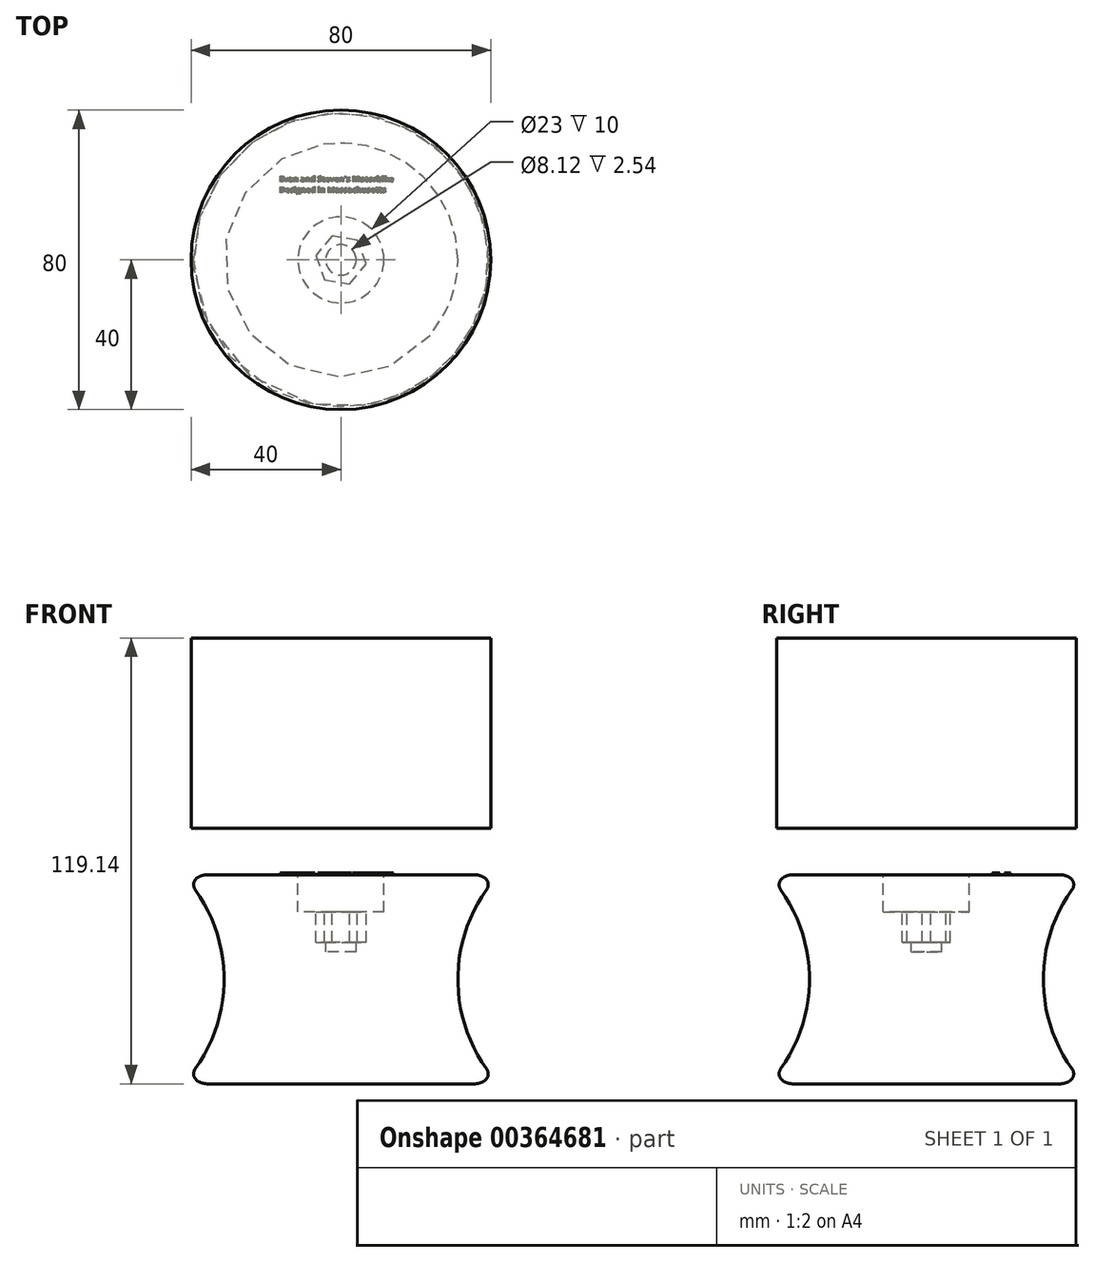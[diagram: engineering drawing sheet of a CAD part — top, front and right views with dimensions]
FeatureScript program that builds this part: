
annotation { "Feature Type Name" : "Feature", "Feature Type Description" : "" }
export const myFeature = defineFeature(function(context is Context, id is Id, definition is map)
    precondition{}
    {
        {
            var Q0;
            Q0=qCreatedBy(makeId("Top.planeOp"),FACE);
            var sketch = newSketch(context, id + "F0", { "sketchPlane" : qUnion([Q0])});
            skCircle(sketch, "E0", {"center": v(0, 0) * mm, "radius": 40 * mm});
            skCircle(sketch, "E1.cCircle", {"center": v(0, 0) * mm, "radius": 5.92 * mm, "construction": true});
            skLineSegment(sketch, "E1.0", {"start": v(-2.36, 6.42) * mm, "end": v(4.38, 5.25) * mm});
            skLineSegment(sketch, "E1.1", {"start": v(4.38, 5.25) * mm, "end": v(6.74, -1.17) * mm});
            skLineSegment(sketch, "E1.2", {"start": v(6.74, -1.17) * mm, "end": v(2.36, -6.42) * mm});
            skLineSegment(sketch, "E1.3", {"start": v(2.36, -6.42) * mm, "end": v(-4.38, -5.25) * mm});
            skLineSegment(sketch, "E1.4", {"start": v(-4.38, -5.25) * mm, "end": v(-6.74, 1.17) * mm});
            skLineSegment(sketch, "E1.5", {"start": v(-6.74, 1.17) * mm, "end": v(-2.36, 6.42) * mm});
            skPoint(sketch, "E1.0.midPoint", {"position": v(1.01, 5.84) * mm});
            skSolve(sketch);
        }
        {
            var Q0;
            Q0=qSketchRegion(id+"F0",true);
            var Q1;
            Q1=makeQuery(id+"F0.imprint","IMPRINT",FACE,{"disambiguationData":[TD([[makeQuery(id+"F0.imprint","IMPRINT",EDGE,{"derivedFrom":sQuery(id+"F0.wireOp",EDGE,"E1.0")}),-1.0]])]});
            extrude(context, id + "F1", {"entities" : qUnion([Q0, Q1]), "depth" : 50.8 * mm});
        }
        {
            var Q0;
            Q0=makeQuery(id+"F1.opExtrude","CAP_FACE",FACE,{"disambiguationData":[OSD([sQuery(id+"F0.wireOp",EDGE,"E0"),sQuery(id+"F0.wireOp",EDGE,"E1.0"),sQuery(id+"F0.wireOp",EDGE,"E1.1"),sQuery(id+"F0.wireOp",EDGE,"E1.2"),sQuery(id+"F0.wireOp",EDGE,"E1.3"),sQuery(id+"F0.wireOp",EDGE,"E1.4"),sQuery(id+"F0.wireOp",EDGE,"E1.5")])],"isStart":true});
            var sketch = newSketch(context, id + "F2", { "sketchPlane" : qUnion([Q0])});
            skCircle(sketch, "E2", {"center": v(0, 0) * mm, "radius": 11.5 * mm});
            skSolve(sketch);
        }
        {
            var Q0;
            Q0=qCreatedBy(makeId("Right.planeOp"),FACE);
            var sketch = newSketch(context, id + "F3", { "sketchPlane" : qUnion([Q0])});
            skLineSegment(sketch, "E3.left", {"start": v(-40, -12.46) * mm, "end": v(-40, -68.34) * mm});
            skArc(sketch, "E4", {"start": v(-40, -65.8) * mm, "mid": v(-31.22, -40.4) * mm, "end": v(-40, -15) * mm});
            skLineSegment(sketch, "E5.bottom", {"start": v(-40, -12.46) * mm, "end": v(0, -12.46) * mm});
            skLineSegment(sketch, "E5.top", {"start": v(-40, -68.34) * mm, "end": v(0, -68.34) * mm});
            skLineSegment(sketch, "E5.right", {"start": v(0, -12.46) * mm, "end": v(0, -68.34) * mm});
            skSolve(sketch);
        }
        {
            var Q0;
            {var subQ1=sQuery(id+"F3.wireOp",EDGE,"E4");Q0=makeQuery(id+"F3.imprint","IMPRINT",FACE,{"disambiguationData":[TD([[makeQuery(id+"F3.imprint","IMPRINT",EDGE,{"derivedFrom":subQ1}),-1.0]])]});}
            var Q1;
            Q1=sQuery(id+"F3.wireOp",EDGE,"E5.right");
            revolve(context, id + "F4", {"entities" : qUnion([Q0]), "axis" : qUnion([Q1]), "revolveType" : RevolveType.FULL});
        }
        {
            var Q0;
            Q0=makeQuery(id+"F4.opRevolve","SWEPT_FACE",FACE,{"disambiguationData":[OSD([sQuery(id+"F3.wireOp",EDGE,"E5.bottom")])]});
            var sketch = newSketch(context, id + "F5", { "sketchPlane" : qUnion([Q0])});
            skLineSegment(sketch, "E6.0.0", {"start": v(-2.36, 6.42) * mm, "end": v(-6.74, 1.17) * mm});
            skLineSegment(sketch, "E6.0.1", {"start": v(-6.74, 1.17) * mm, "end": v(-4.38, -5.25) * mm});
            skLineSegment(sketch, "E6.0.2", {"start": v(-4.38, -5.25) * mm, "end": v(2.36, -6.42) * mm});
            skLineSegment(sketch, "E6.0.3", {"start": v(2.36, -6.42) * mm, "end": v(6.74, -1.17) * mm});
            skLineSegment(sketch, "E6.0.4", {"start": v(6.74, -1.17) * mm, "end": v(4.38, 5.25) * mm});
            skLineSegment(sketch, "E6.0.5", {"start": v(4.38, 5.25) * mm, "end": v(-2.36, 6.42) * mm});
            skCircle(sketch, "E7.0", {"center": v(0, 0) * mm, "radius": 11.5 * mm});
            skCircle(sketch, "E8", {"center": v(0, 0) * mm, "radius": 4.06 * mm});
            skText(sketch, "E9", { "text": "Evan & Steven\'s Capstone", "fontName": "OpenSans-Bold.ttf"});
            const initialGuessF5  = {"E9": [-0.01963, 0.0219, 1, 0, 0.00215]};
            skSetInitialGuess(sketch, initialGuessF5);
            skSolve(sketch);
        }
        {
            var Q0;
            Q0=makeQuery(id+"F5.imprint","IMPRINT",FACE,{"disambiguationData":[TD([[makeQuery(id+"F5.imprint","IMPRINT",EDGE,{"derivedFrom":sQuery(id+"F5.wireOp",EDGE,"E6.0.0")}),1.0]])]});
            extrude(context, id + "F6", {"entities" : qUnion([Q0]), "operationType" : NewBodyOperationType.REMOVE, "oppositeDirection" : true, "depth" : 18.03 * mm});
        }
        {
            var Q0;
            Q0=makeQuery(id+"F5.imprint","IMPRINT",FACE,{"disambiguationData":[TD([[makeQuery(id+"F5.imprint","IMPRINT",EDGE,{"derivedFrom":sQuery(id+"F5.wireOp",EDGE,"E6.0.0")}),-1.0]])]});
            extrude(context, id + "F7", {"entities" : qUnion([Q0]), "operationType" : NewBodyOperationType.REMOVE, "oppositeDirection" : true, "depth" : 10 * mm});
        }
        {
            var Q0;
            Q0=makeQuery(id+"F6.boolean.opBoolean","SPLIT",FACE,{"disambiguationData":[TD([makeQuery(id+"F6.opExtrude","SWEPT_FACE",FACE,{"disambiguationData":[OSD([sQuery(id+"F5.wireOp",EDGE,"E8")])]})])],"derivedFrom":makeQuery(id+"F4.opRevolve","SWEPT_FACE",FACE,{"disambiguationData":[OSD([sQuery(id+"F3.wireOp",EDGE,"E5.bottom")])]})});
            extrude(context, id + "F8", {"entities" : qUnion([Q0]), "operationType" : NewBodyOperationType.REMOVE, "oppositeDirection" : true, "depth" : 20.57 * mm});
        }
        {
            var Q0;
            Q0=makeQuery(id+"F4.opRevolve","SWEPT_EDGE",EDGE,{"disambiguationData":[OSD([sQuery(id+"F3.wireOp",EDGE,"E5.bottom"),sQuery(id+"F3.wireOp",EDGE,"E3.left")])]});
            var Q1;
            Q1=makeQuery(id+"F4.opRevolve","SWEPT_EDGE",EDGE,{"disambiguationData":[OSD([sQuery(id+"F3.wireOp",EDGE,"E5.top"),sQuery(id+"F3.wireOp",EDGE,"E3.left")])]});
            fillet(context, id + "F9", {"entities" : qUnion([Q0, Q1]), "radius" : 5.08 * mm, "tangentPropagation" : true, "allowEdgeOverflow" : false});
        }
        {
            var Q0;
            Q0=makeQuery(id+"F4.opRevolve","SWEPT_FACE",FACE,{"disambiguationData":[OSD([sQuery(id+"F3.wireOp",EDGE,"E4")])]});
            fillet(context, id + "F10", {"entities" : qUnion([Q0]), "radius" : 2.25 * mm, "tangentPropagation" : true, "allowEdgeOverflow" : false});
        }
        {
            var Q0;
            {var subQ1=sQuery(id+"F3.wireOp",EDGE,"E5.bottom");Q0=makeQuery(id+"F6.boolean.opBoolean","SPLIT",FACE,{"disambiguationData":[TD([makeQuery(id+"F6.opExtrude","SWEPT_FACE",FACE,{"disambiguationData":[OSD([sQuery(id+"F5.wireOp",EDGE,"E6.0.0")])]})])],"derivedFrom":makeQuery(id+"F4.opRevolve","SWEPT_FACE",FACE,{"disambiguationData":[OSD([subQ1])]})});}
            var sketch = newSketch(context, id + "F11", { "sketchPlane" : qUnion([Q0])});
            skText(sketch, "E10", { "text": "Evan and Steven\'s Motorbike\nDesigned in Massachusetts", "fontName": "OpenSans-Bold.ttf"});
            const initialGuessF11  = {"E10": [-0.01643, 0.02087, 1, 0, 0.00152]};
            skSetInitialGuess(sketch, initialGuessF11);
            skSolve(sketch);
        }
        {
            var Q0;
            Q0 = qSketchRegion(id + "F11", true);
            extrude(context, id + "F12", {"entities" : qUnion([Q0]), "operationType" : NewBodyOperationType.ADD, "depth" : 0.5 * mm});
        }
    });
